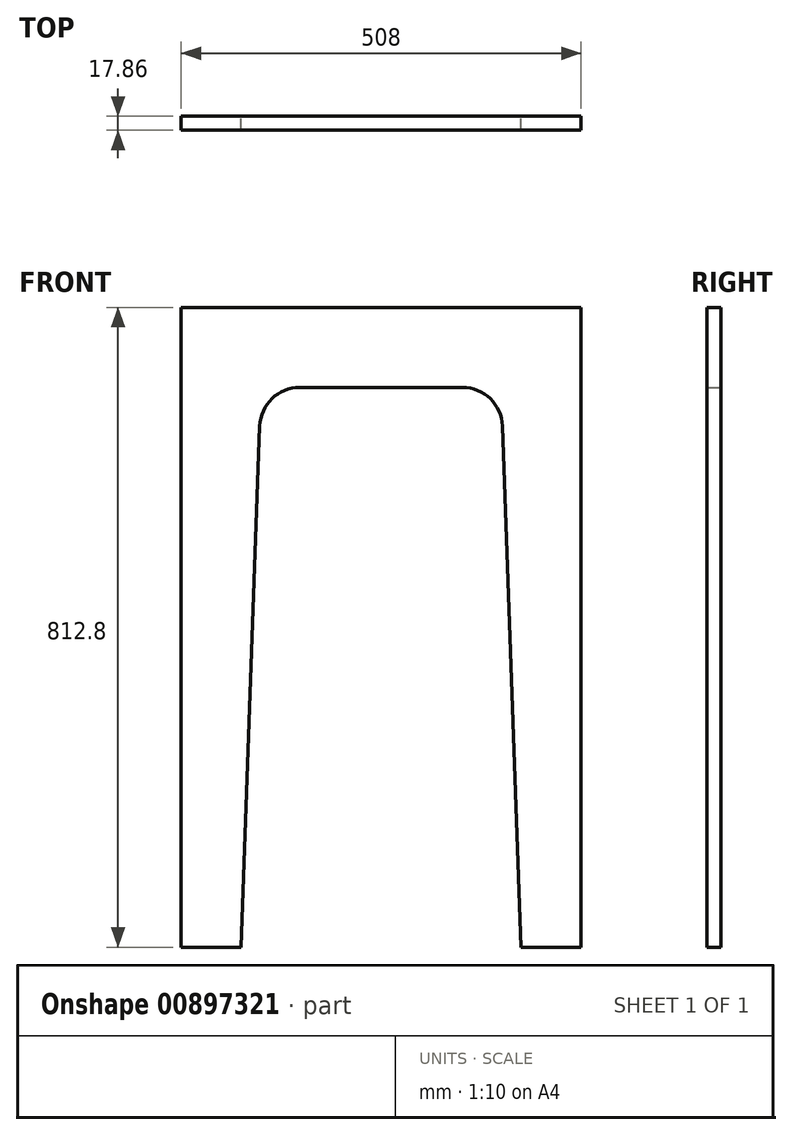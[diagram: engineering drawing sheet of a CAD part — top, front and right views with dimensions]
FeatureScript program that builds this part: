
annotation { "Feature Type Name" : "Feature", "Feature Type Description" : "" }
export const myFeature = defineFeature(function(context is Context, id is Id, definition is map)
    precondition{}
    {
        {
            var Q0;
            Q0=qCreatedBy(makeId("Front.planeOp"),FACE);
            var sketch = newSketch(context, id + "F0", { "sketchPlane" : qUnion([Q0])});
            skLineSegment(sketch, "E0", {"start": v(-254, 471.31) * mm, "end": v(254, 471.31) * mm});
            skLineSegment(sketch, "E1", {"start": v(254, 471.31) * mm, "end": v(254, -341.49) * mm});
            skLineSegment(sketch, "E2", {"start": v(254, -341.49) * mm, "end": v(177.8, -341.49) * mm});
            skLineSegment(sketch, "E3", {"start": v(177.8, -341.49) * mm, "end": v(154.15, 320.73) * mm});
            skLineSegment(sketch, "E4", {"start": v(103.38, 369.71) * mm, "end": v(-103.38, 369.71) * mm});
            skLineSegment(sketch, "E5", {"start": v(-154.15, 320.73) * mm, "end": v(-177.8, -341.49) * mm});
            skLineSegment(sketch, "E6", {"start": v(-177.8, -341.49) * mm, "end": v(-254, -341.49) * mm});
            skLineSegment(sketch, "E7", {"start": v(-254, -341.49) * mm, "end": v(-254, 471.31) * mm});
            skPoint(sketch, "E8.visualSharp", {"position": v(-152.4, 369.71) * mm});
            skArc(sketch, "E8.filletArc", {"start": v(-103.38, 369.71) * mm, "mid": v(-138.66, 355.47) * mm, "end": v(-154.15, 320.73) * mm});
            skPoint(sketch, "E9.visualSharp", {"position": v(152.4, 369.71) * mm});
            skArc(sketch, "E9.filletArc", {"start": v(154.15, 320.73) * mm, "mid": v(138.66, 355.47) * mm, "end": v(103.38, 369.71) * mm});
            skSolve(sketch);
        }
        {
            var Q0;
            Q0 = qSketchRegion(id + "F0", true);
            extrude(context, id + "F1", {"entities" : qUnion([Q0]), "depth" : 17.86 * mm, "offsetDistance" : 25.4 * mm});
        }
    });
